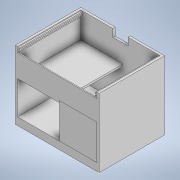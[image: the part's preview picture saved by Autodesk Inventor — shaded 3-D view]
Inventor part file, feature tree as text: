
AUTODESK INVENTOR PART (.ipt)
format: ipt  version: 2022 (Build 260153000, 153)  size: 196,608 bytes
history: native  units: mm
features: sketch x9, extrude x8
ambient origin geometry x8: Origin, YZ Plane, XZ Plane, XY Plane, X Axis, Y Axis, Z Axis, Center Point
bodies: Body1 (feature_tree)
feature tree (17):
  extrude  "Extrusion6"  Depth=86.0mm
  extrude  "Extrusion7"  Depth=80.0mm TaperAngle=0.0deg
  extrude  "Extrusion8"  Depth=10.0mm
  extrude  "Extrusion9"  Depth=80.0mm TaperAngle=0.0deg
  extrude  "Extrusion10"  Depth=1.5mm
  extrude  "Extrusion11"  Depth=2.0mm TaperAngle=0.0deg
  extrude  "Extrusion12"  Depth=1.5mm
  extrude  "Extrusion13"  Depth=2.0mm TaperAngle=0.0deg
  sketch  "Sketch20"  dims[d50=31.0mm d51=2.5mm d52=55.0mm d53=0.0mm d54=1.25mm d55=26.971mm d56=55.0mm d57=0.0mm d58=10.0mm d59=0.0mm]
  sketch  "Sketch12"  dims[d23=110.0mm d24=86.0mm]
  sketch  "Sketch13"  dims[d25=10.0mm d26=0.0mm d30=80.0mm d31=0.0mm]
  sketch  "Sketch14"  dims[d33=20.0mm d34=10.0mm]
  sketch  "Sketch15"  dims[d35=20.0mm d36=80.0mm d37=0.0mm]
  sketch  "Sketch16"  dims[d39=1.5mm d40=1.5mm]
  sketch  "Sketch17"  dims[d41=1.5mm d42=2.0mm d43=0.0mm]
  sketch  "Sketch18"  dims[d45=1.5mm d46=1.5mm]
  sketch  "Sketch19"  dims[d47=1.5mm d48=2.0mm d49=0.0mm]
